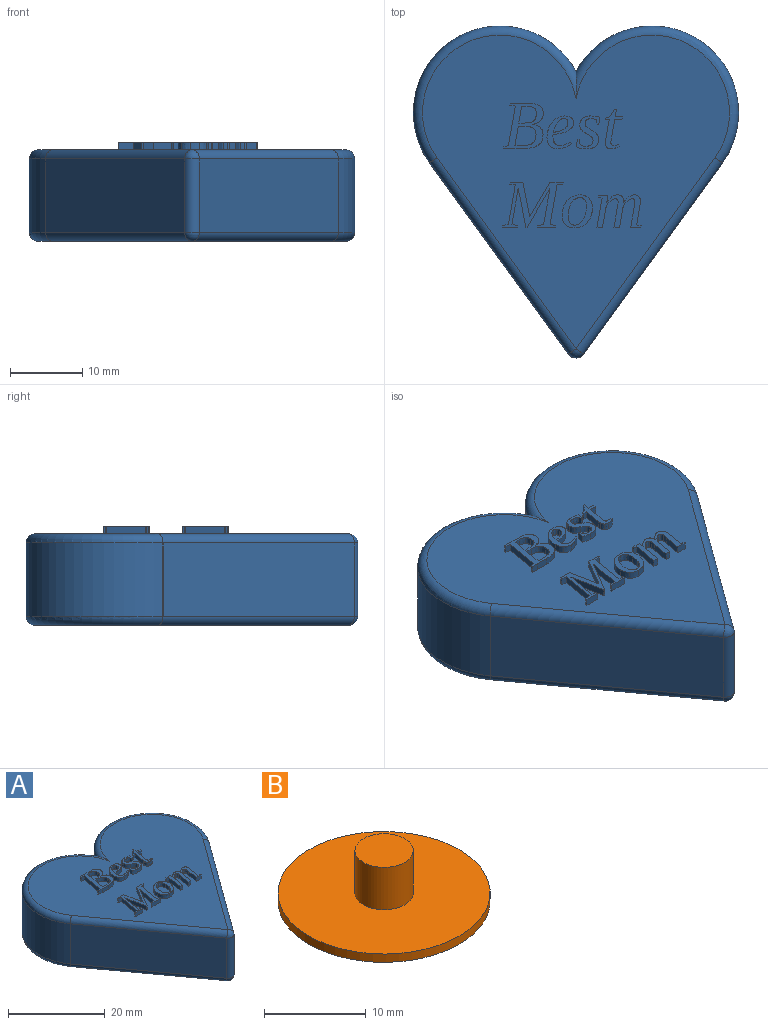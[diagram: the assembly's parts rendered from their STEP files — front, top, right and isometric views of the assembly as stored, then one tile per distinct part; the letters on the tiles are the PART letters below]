
ASSEMBLY  parts=2 mates=1
PART A: 218 faces, bbox 47.1x47x13.7 mm
  f0: plane 43.51x42.6mm, normal (0,0,1), area 1042mm2, adj f10,f12,f13,f14,f23,f24,f25,f26
  f1: plane 26.52x19.29mm, normal (-0.81,-0.59,0), area 333.2mm2, adj f6,f9,f10,f17
  f2: plane 26.52x19.29mm, normal (0.81,-0.59,0), area 333.2mm2, adj f6,f7,f12,f18
  f3: cylinder r=12.01mm len=22.57mm, axis (0,0,-1), area 398.6mm2, adj f4,f14,f18,f22
  f4: cylinder r=12.01mm len=22.57mm, axis (0,0,-1), area 398.6mm2, adj f3,f13,f17,f21
  f5: plane 43.51x42.6mm, normal (0,0,-1), area 785.1mm2, adj f7,f9,f21,f22,f214
  f6: cylinder r=1.27mm len=10.16mm, axis (0,0,-1), area 24.3mm2, adj f1,f2,f8,f11
  f7: cylinder r=1.27mm len=27.27mm, axis (0.59,0.81,0), area 65.4mm2, adj f2,f5,f8,f20
  f8: sphere r=1.27mm, area 3mm2, adj f6,f7,f9
  f9: cylinder r=1.27mm len=27.27mm, axis (0.59,-0.81,0), area 65.4mm2, adj f1,f5,f8,f19
  f10: cylinder r=1.27mm len=27.27mm, axis (-0.59,0.81,0), area 65.4mm2, adj f0,f1,f11,f15
  f11: sphere r=1.27mm, area 3mm2, adj f6,f10,f12
  f12: cylinder r=1.27mm len=27.27mm, axis (-0.59,-0.81,0), area 65.4mm2, adj f0,f2,f11,f16
  f13: torus R=10.74mm, axis (0,0,1), area 77.3mm2, adj f0,f4,f14,f15
  f14: torus R=10.74mm, axis (0,0,1), area 77.3mm2, adj f0,f3,f13,f16
  f15: sphere r=1.27mm, area 0mm2, adj f10,f13,f17
  f16: sphere r=1.27mm, area 0mm2, adj f12,f14,f18
  f17: cylinder r=1.27mm len=10.16mm, axis (0,0,-1), area 0.1mm2, adj f1,f4,f15,f19
  f18: cylinder r=1.27mm len=10.16mm, axis (0,0,-1), area 0.1mm2, adj f2,f3,f16,f20
  f19: sphere r=1.27mm, area 0mm2, adj f9,f17,f21
  f20: sphere r=1.27mm, area 0mm2, adj f7,f18,f22
  f21: torus R=10.74mm, axis (0,0,1), area 77.3mm2, adj f4,f5,f19,f22
  f22: torus R=10.74mm, axis (0,0,1), area 77.3mm2, adj f3,f5,f20,f21
  f23: plane 1x0.25mm, normal (-0.98,0.19,0), area 0.3mm2, adj f0,f24,f51,f52
  f24: plane 1x0.99mm, normal (0,-1,0), area 1mm2, adj f0,f23,f25,f52
  f25: plane 1.78x1mm, normal (-0.02,-1,0), area 1.8mm2, adj f0,f24,f26,f52
  f26: extruded ~2.03x1mm, area 2.1mm2, adj f0,f25,f27,f52
  f27: extruded ~1.47x1mm, area 1.7mm2, adj f0,f26,f28,f52
  f28: extruded ~1x0.98mm, area 1.1mm2, adj f0,f27,f29,f52
  f29: extruded ~1.12x1mm, area 1.2mm2, adj f0,f28,f30,f52
  f30: extruded ~1.15x1mm, area 1.3mm2, adj f0,f29,f31,f52
  f31: extruded ~1.08x1mm, area 1.2mm2, adj f0,f30,f32,f52
  f32: extruded ~2.06x1.31mm, area 2.8mm2, adj f0,f31,f33,f52
  f33: plane 2.56x1mm, normal (0,1,0), area 2.6mm2, adj f0,f32,f34,f52
  f34: plane 1x0.25mm, normal (-0.98,0.19,0), area 0.3mm2, adj f0,f33,f35,f52
  f35: plane 1x0.78mm, normal (-0.15,-0.99,0), area 0.8mm2, adj f0,f34,f36,f52
  f36: plane 5.5x1mm, normal (-0.98,0.17,0), area 5.6mm2, adj f0,f35,f51,f52
  f37: extruded ~1.31x1mm, area 1.4mm2, adj f38,f49,f52,f54
  f38: extruded ~1.2x1mm, area 1.2mm2, adj f37,f39,f52,f54
  f39: plane 2.67x1mm, normal (0.99,-0.17,0), area 2.7mm2, adj f38,f40,f52,f54
  f40: plane 1x0.86mm, normal (0,-1,0), area 0.9mm2, adj f39,f41,f52,f54
  f41: extruded ~1.19x1mm, area 1.2mm2, adj f40,f42,f52,f54
  f42: extruded ~1x0.92mm, area 1mm2, adj f41,f49,f52,f54
  f43: extruded ~1.29x1mm, area 1.3mm2, adj f44,f50,f52,f53
  f44: plane 1x0.77mm, normal (0,1,0), area 0.8mm2, adj f43,f45,f52,f53
  f45: plane 2.31x1mm, normal (0.98,-0.17,0), area 2.3mm2, adj f44,f46,f52,f53
  f46: plane 1x0.74mm, normal (0,-1,0), area 0.7mm2, adj f45,f47,f52,f53
  f47: extruded ~1x1mm, area 1mm2, adj f46,f48,f52,f53
  f48: extruded ~1x0.72mm, area 0.8mm2, adj f47,f50,f52,f53
  f49: extruded ~1.15x1mm, area 1.3mm2, adj f37,f42,f52,f54
  f50: extruded ~1.06x1mm, area 1.2mm2, adj f43,f48,f52,f53
  f51: plane 1x0.62mm, normal (-0.2,0.98,0), area 0.6mm2, adj f0,f23,f36,f52
  f52: plane 6.27x5.52mm, normal (0,0,1), area 14.1mm2, adj f23,f24,f25,f26,f27,f28,f29,f30
  f53: plane 2.44x2.31mm, normal (0,0,1), area 4.7mm2, adj f43,f44,f45,f46,f47,f48,f50
  f54: plane 2.93x2.7mm, normal (0,0,1), area 6.6mm2, adj f37,f38,f39,f40,f41,f42,f49
  f55: extruded ~1.47x1mm, area 1.6mm2, adj f56,f78,f79,f80
  f56: extruded ~1x0.94mm, area 1mm2, adj f55,f57,f79,f80
  f57: extruded ~1x0.71mm, area 0.9mm2, adj f56,f58,f79,f80
  f58: extruded ~1x0.63mm, area 0.7mm2, adj f57,f59,f79,f80
  f59: extruded ~1x0.41mm, area 0.5mm2, adj f58,f60,f79,f80
  f60: extruded ~1x0.43mm, area 0.5mm2, adj f59,f78,f79,f80
  f61: extruded ~1.08x1mm, area 1.4mm2, adj f0,f62,f77,f79
  f62: extruded ~1x0.69mm, area 0.8mm2, adj f0,f61,f63,f79
  f63: extruded ~1x0.92mm, area 1mm2, adj f0,f62,f64,f79
  f64: extruded ~1.22x1mm, area 1.3mm2, adj f0,f63,f65,f79
  f65: extruded ~1.09x1mm, area 1.4mm2, adj f0,f64,f66,f79
  f66: extruded ~1.45x1mm, area 1.5mm2, adj f0,f65,f67,f79
  f67: extruded ~1.21x1mm, area 1.3mm2, adj f0,f66,f68,f79
  f68: extruded ~1.16x1mm, area 1.3mm2, adj f0,f67,f69,f79
  f69: extruded ~1x0.91mm, area 0.9mm2, adj f0,f68,f70,f79
  f70: extruded ~1x0.91mm, area 1.1mm2, adj f0,f69,f71,f79
  f71: plane 1x0.2mm, normal (0.82,0.57,0), area 0.2mm2, adj f0,f70,f72,f79
  f72: extruded ~1x0.66mm, area 0.7mm2, adj f0,f71,f73,f79
  f73: extruded ~1x0.77mm, area 0.8mm2, adj f0,f72,f74,f79
  f74: extruded ~1x0.74mm, area 0.8mm2, adj f0,f73,f75,f79
  f75: extruded ~1x0.89mm, area 0.9mm2, adj f0,f74,f76,f79
  f76: plane 1x0.34mm, normal (1,-0.06,0), area 0.3mm2, adj f0,f75,f77,f79
  f77: extruded ~2.1x1mm, area 2.2mm2, adj f0,f61,f76,f79
  f78: extruded ~1x0.89mm, area 1.1mm2, adj f55,f60,f79,f80
  f79: plane 4.58x3.72mm, normal (0,0,1), area 6.7mm2, adj f55,f56,f57,f58,f59,f60,f61,f62
  f80: plane 2.03x1.92mm, normal (0,0,1), area 2.4mm2, adj f55,f56,f57,f58,f59,f60,f78
  f81: extruded ~1.04x1mm, area 1.2mm2, adj f0,f82,f106,f107
  f82: extruded ~1x0.66mm, area 0.7mm2, adj f0,f81,f83,f107
  f83: extruded ~1x0.71mm, area 0.9mm2, adj f0,f82,f84,f107
  f84: extruded ~1x0.74mm, area 0.9mm2, adj f0,f83,f85,f107
  f85: extruded ~1x0.44mm, area 0.5mm2, adj f0,f84,f86,f107
  f86: extruded ~1x0.54mm, area 0.6mm2, adj f0,f85,f87,f107
  f87: extruded ~1x0.61mm, area 0.6mm2, adj f0,f86,f88,f107
  f88: extruded ~1x0.77mm, area 0.8mm2, adj f0,f87,f89,f107
  f89: plane 1x0.5mm, normal (-0.99,-0.13,0), area 0.5mm2, adj f0,f88,f90,f107
  f90: plane 1x0.22mm, normal (0,-1,0), area 0.2mm2, adj f0,f89,f91,f107
  f91: plane 1x0.97mm, normal (0.98,-0.17,0), area 1mm2, adj f0,f90,f92,f107
  f92: extruded ~1.25x1mm, area 1.3mm2, adj f0,f91,f93,f107
  f93: extruded ~1.15x1mm, area 1.2mm2, adj f0,f92,f94,f107
  f94: extruded ~1x0.95mm, area 1.1mm2, adj f0,f93,f95,f107
  f95: extruded ~1x0.65mm, area 0.7mm2, adj f0,f94,f96,f107
  f96: extruded ~1x0.7mm, area 0.9mm2, adj f0,f95,f97,f107
  f97: extruded ~1x0.7mm, area 0.8mm2, adj f0,f96,f98,f107
  f98: extruded ~1x0.49mm, area 0.5mm2, adj f0,f97,f99,f107
  f99: extruded ~1.02x1mm, area 1.5mm2, adj f0,f98,f100,f107
  f100: extruded ~1x0.5mm, area 0.5mm2, adj f0,f99,f101,f107
  f101: extruded ~1x0.34mm, area 0.4mm2, adj f0,f100,f102,f107
  f102: plane 1x0.64mm, normal (0.99,0.12,0), area 0.6mm2, adj f0,f101,f103,f107
  f103: plane 1x0.21mm, normal (0,1,0), area 0.2mm2, adj f0,f102,f104,f107
  f104: plane 1.05x1mm, normal (-0.98,0.18,0), area 1.1mm2, adj f0,f103,f105,f107
  f105: extruded ~1.3x1mm, area 1.3mm2, adj f0,f104,f106,f107
  f106: extruded ~1.35x1mm, area 1.4mm2, adj f0,f81,f105,f107
  f107: plane 4.58x3.3mm, normal (0,0,1), area 5.8mm2, adj f81,f82,f83,f84,f85,f86,f87,f88
  f108: extruded ~1x0.31mm, area 0.3mm2, adj f0,f109,f127,f128
  f109: extruded ~1x0.62mm, area 0.6mm2, adj f0,f108,f110,f128
  f110: plane 2.55x1mm, normal (0.98,-0.17,0), area 2.6mm2, adj f0,f109,f111,f128
  f111: plane 1x1mm, normal (0,-1,0), area 1mm2, adj f0,f110,f112,f128
  f112: plane 1x0.39mm, normal (0.98,-0.19,0), area 0.4mm2, adj f0,f111,f113,f128
  f113: plane 1x1mm, normal (0,1,0), area 1mm2, adj f0,f112,f114,f128
  f114: plane 1x0.99mm, normal (0.99,-0.17,0), area 1mm2, adj f0,f113,f115,f128
  f115: plane 1x0.3mm, normal (0,1,0), area 0.3mm2, adj f0,f114,f116,f128
  f116: plane 1x0.99mm, normal (-0.84,0.54,0), area 1.2mm2, adj f0,f115,f117,f128
  f117: plane 1x0.62mm, normal (-0.28,0.96,0), area 0.6mm2, adj f0,f116,f118,f128
  f118: plane 1x0.21mm, normal (-0.98,0.17,0), area 0.2mm2, adj f0,f117,f119,f128
  f119: plane 1x0.57mm, normal (0,-1,0), area 0.6mm2, adj f0,f118,f120,f128
  f120: extruded ~2.91x1mm, area 3mm2, adj f0,f119,f121,f128
  f121: extruded ~1x0.32mm, area 0.3mm2, adj f0,f120,f122,f128
  f122: extruded ~1x0.62mm, area 0.7mm2, adj f0,f121,f123,f128
  f123: extruded ~1x0.58mm, area 0.6mm2, adj f0,f122,f124,f128
  f124: extruded ~1.16x1mm, area 1.2mm2, adj f0,f123,f125,f128
  f125: plane 1x0.22mm, normal (0.91,0.41,0), area 0.2mm2, adj f0,f124,f126,f128
  f126: extruded ~1x0.71mm, area 0.7mm2, adj f0,f125,f127,f128
  f127: extruded ~1x0.27mm, area 0.3mm2, adj f0,f108,f126,f128
  f128: plane 5.46x2.42mm, normal (0,0,1), area 4.9mm2, adj f108,f109,f110,f111,f112,f113,f114,f115
  f129: plane 1x0.16mm, normal (0,-1,0), area 0.2mm2, adj f0,f130,f153,f154
  f130: plane 5.36x3.17mm, normal (0.86,-0.51,0), area 6.2mm2, adj f0,f129,f131,f154
  f131: plane 4.99x1mm, normal (-0.98,0.17,0), area 5.1mm2, adj f0,f130,f132,f154
  f132: plane 1x0.86mm, normal (-0.14,0.99,0), area 0.9mm2, adj f0,f131,f133,f154
  f133: plane 1x0.25mm, normal (-0.98,0.19,0), area 0.3mm2, adj f0,f132,f134,f154
  f134: plane 2.53x1mm, normal (0,-1,0), area 2.5mm2, adj f0,f133,f135,f154
  f135: plane 1x0.25mm, normal (0.98,-0.19,0), area 0.3mm2, adj f0,f134,f136,f154
  f136: plane 1x0.78mm, normal (0.16,0.99,0), area 0.8mm2, adj f0,f135,f137,f154
  f137: plane 5.5x1mm, normal (0.98,-0.17,0), area 5.6mm2, adj f0,f136,f138,f154
  f138: plane 1x0.82mm, normal (0.15,-0.99,0), area 0.8mm2, adj f0,f137,f139,f154
  f139: plane 1x0.25mm, normal (0.98,-0.18,0), area 0.3mm2, adj f0,f138,f140,f154
  f140: plane 1.87x1mm, normal (0,1,0), area 1.9mm2, adj f0,f139,f141,f154
  f141: plane 4.76x2.78mm, normal (-0.86,0.5,0), area 5.5mm2, adj f0,f140,f142,f154
  f142: plane 4.76x1mm, normal (0.98,0.2,0), area 4.9mm2, adj f0,f141,f143,f154
  f143: plane 1.78x1mm, normal (0,1,0), area 1.8mm2, adj f0,f142,f144,f154
  f144: plane 1x0.25mm, normal (-0.98,0.19,0), area 0.3mm2, adj f0,f143,f145,f154
  f145: plane 1x0.78mm, normal (-0.15,-0.99,0), area 0.8mm2, adj f0,f144,f146,f154
  f146: plane 5.5x1mm, normal (-0.98,0.17,0), area 5.6mm2, adj f0,f145,f147,f154
  f147: plane 1x0.81mm, normal (-0.15,0.99,0), area 0.8mm2, adj f0,f146,f148,f154
  f148: plane 1x0.25mm, normal (-0.98,0.18,0), area 0.3mm2, adj f0,f147,f149,f154
  f149: plane 2.12x1mm, normal (0,-1,0), area 2.1mm2, adj f0,f148,f150,f154
  f150: plane 1x0.25mm, normal (0.98,-0.18,0), area 0.3mm2, adj f0,f149,f151,f154
  f151: plane 1x0.82mm, normal (0.15,0.99,0), area 0.8mm2, adj f0,f150,f152,f154
  f152: plane 4.99x1mm, normal (0.98,-0.17,0), area 5.1mm2, adj f0,f151,f153,f154
  f153: plane 5.36x1.07mm, normal (-0.98,-0.2,0), area 5.5mm2, adj f0,f129,f152,f154
  f154: plane 8.48x6.24mm, normal (0,0,1), area 17.3mm2, adj f129,f130,f131,f132,f133,f134,f135,f136
  f155: extruded ~1.24x1mm, area 1.4mm2, adj f0,f156,f174,f175
  f156: extruded ~1.28x1mm, area 1.4mm2, adj f0,f155,f157,f175
  f157: extruded ~1x1mm, area 1.4mm2, adj f0,f156,f158,f175
  f158: extruded ~1.39x1mm, area 1.4mm2, adj f0,f157,f159,f175
  f159: extruded ~1.34x1mm, area 1.5mm2, adj f0,f158,f160,f175
  f160: extruded ~1.24x1mm, area 1.4mm2, adj f0,f159,f161,f175
  f161: extruded ~1.28x1mm, area 1.4mm2, adj f0,f160,f162,f175
  f162: extruded ~1x1mm, area 1.4mm2, adj f0,f161,f163,f175
  f163: extruded ~1.39x1mm, area 1.4mm2, adj f0,f162,f174,f175
  f164: extruded ~1x0.96mm, area 1mm2, adj f165,f173,f175,f176
  f165: extruded ~1.28x1mm, area 1.3mm2, adj f164,f166,f175,f176
  f166: extruded ~1x0.93mm, area 1.1mm2, adj f165,f167,f175,f176
  f167: extruded ~1x0.8mm, area 0.9mm2, adj f166,f168,f175,f176
  f168: extruded ~1x0.7mm, area 0.8mm2, adj f167,f169,f175,f176
  f169: extruded ~1x0.97mm, area 1mm2, adj f168,f170,f175,f176
  f170: extruded ~1.26x1mm, area 1.3mm2, adj f169,f171,f175,f176
  f171: extruded ~1x0.93mm, area 1.1mm2, adj f170,f172,f175,f176
  f172: extruded ~1x0.81mm, area 0.9mm2, adj f171,f173,f175,f176
  f173: extruded ~1x0.68mm, area 0.8mm2, adj f164,f172,f175,f176
  f174: extruded ~1.34x1mm, area 1.5mm2, adj f0,f155,f163,f175
  f175: plane 4.58x4.19mm, normal (0,0,1), area 7.6mm2, adj f155,f156,f157,f158,f159,f160,f161,f162
  f176: plane 3.84x2.56mm, normal (0,0,1), area 7.6mm2, adj f164,f165,f166,f167,f168,f169,f170,f171
  f177: extruded ~1x0.74mm, area 1mm2, adj f0,f178,f212,f213
  f178: extruded ~1x0.76mm, area 0.8mm2, adj f0,f177,f179,f213
  f179: extruded ~1x0.63mm, area 0.7mm2, adj f0,f178,f180,f213
  f180: extruded ~1x0.76mm, area 0.8mm2, adj f0,f179,f181,f213
  f181: extruded ~1x0.74mm, area 1mm2, adj f0,f180,f182,f213
  f182: plane 1x0.9mm, normal (0.99,-0.14,0), area 0.9mm2, adj f0,f181,f183,f213
  f183: plane 1.29x1mm, normal (0,1,0), area 1.3mm2, adj f0,f182,f184,f213
  f184: plane 1x0.21mm, normal (-0.98,0.17,0), area 0.2mm2, adj f0,f183,f185,f213
  f185: plane 1x0.55mm, normal (-0.21,-0.98,0), area 0.6mm2, adj f0,f184,f186,f213
  f186: plane 4.05x1mm, normal (-0.98,0.17,0), area 4.1mm2, adj f0,f185,f187,f213
  f187: plane 1x0.77mm, normal (0,-1,0), area 0.8mm2, adj f0,f186,f188,f213
  f188: plane 2.68x1mm, normal (0.99,-0.17,0), area 2.7mm2, adj f0,f187,f189,f213
  f189: extruded ~1x0.56mm, area 0.6mm2, adj f0,f188,f190,f213
  f190: extruded ~1x0.53mm, area 0.7mm2, adj f0,f189,f191,f213
  f191: extruded ~1x0.5mm, area 0.6mm2, adj f0,f190,f192,f213
  f192: extruded ~1x0.32mm, area 0.4mm2, adj f0,f191,f193,f213
  f193: extruded ~1x0.34mm, area 0.4mm2, adj f0,f192,f194,f213
  f194: extruded ~1x0.77mm, area 0.8mm2, adj f0,f193,f195,f213
  f195: plane 2.71x1mm, normal (-0.98,0.17,0), area 2.7mm2, adj f0,f194,f196,f213
  f196: plane 1x0.77mm, normal (0,-1,0), area 0.8mm2, adj f0,f195,f197,f213
  f197: plane 2.68x1mm, normal (0.99,-0.17,0), area 2.7mm2, adj f0,f196,f198,f213
  f198: extruded ~1x0.57mm, area 0.6mm2, adj f0,f197,f199,f213
  f199: extruded ~1x0.51mm, area 0.7mm2, adj f0,f198,f200,f213
  f200: extruded ~1x0.49mm, area 0.5mm2, adj f0,f199,f201,f213
  f201: extruded ~1x0.31mm, area 0.3mm2, adj f0,f200,f202,f213
  f202: extruded ~1x0.34mm, area 0.4mm2, adj f0,f201,f203,f213
  f203: extruded ~1x0.77mm, area 0.8mm2, adj f0,f202,f204,f213
  f204: plane 2.71x1mm, normal (-0.98,0.17,0), area 2.7mm2, adj f0,f203,f205,f213
  f205: plane 1.4x1mm, normal (0,-1,0), area 1.4mm2, adj f0,f204,f206,f213
  f206: plane 1x0.21mm, normal (0.98,-0.19,0), area 0.2mm2, adj f0,f205,f207,f213
  f207: plane 1x0.61mm, normal (0.19,0.98,0), area 0.6mm2, adj f0,f206,f208,f213
  f208: extruded ~2.93x1mm, area 3mm2, adj f0,f207,f209,f213
  f209: extruded ~1x0.27mm, area 0.3mm2, adj f0,f208,f210,f213
  f210: extruded ~1x0.72mm, area 0.8mm2, adj f0,f209,f211,f213
  f211: extruded ~1x0.62mm, area 0.7mm2, adj f0,f210,f212,f213
  f212: extruded ~1x0.77mm, area 0.8mm2, adj f0,f177,f211,f213
  f213: plane 6.13x4.49mm, normal (0,0,1), area 11.8mm2, adj f177,f178,f179,f180,f181,f182,f183,f184
  f214: cylinder r=10.5mm len=21mm, axis (0,0,-1), area 66mm2, adj f5,f215
  f215: plane 21x21mm, normal (0,0,-1), area 62.8mm2, adj f214,f216
  f216: cylinder r=9.5mm len=19mm, axis (0,0,-1), area 304.4mm2, adj f215,f217
  f217: plane 19x19mm, normal (0,0,-1), area 283.5mm2, adj f216
PART B: 5 faces, bbox 20.9x20.9x6.1 mm
  f0: cylinder r=10.45mm len=20.9mm, axis (0,0,-1), area 65.7mm2, adj f1,f2
  f1: plane 20.9x20.9mm, normal (0,0,1), area 317.1mm2, adj f0,f3
  f2: plane 20.9x20.9mm, normal (0,0,-1), area 343.1mm2, adj f0
  f3: cylinder r=2.88mm len=5.75mm, axis (0,0,-1), area 92.1mm2, adj f1,f4
  f4: plane 5.75x5.75mm, normal (0,0,1), area 26mm2, adj f3
PLACE A t=(-7.22,3.76,-0.82)mm
PLACE B t=(-7.22,1.76,-0.82)mm
MATE fastened B.f3 <-> A.f214  axis (0,0,1) through (-7.22,1.76,5.28)mm
